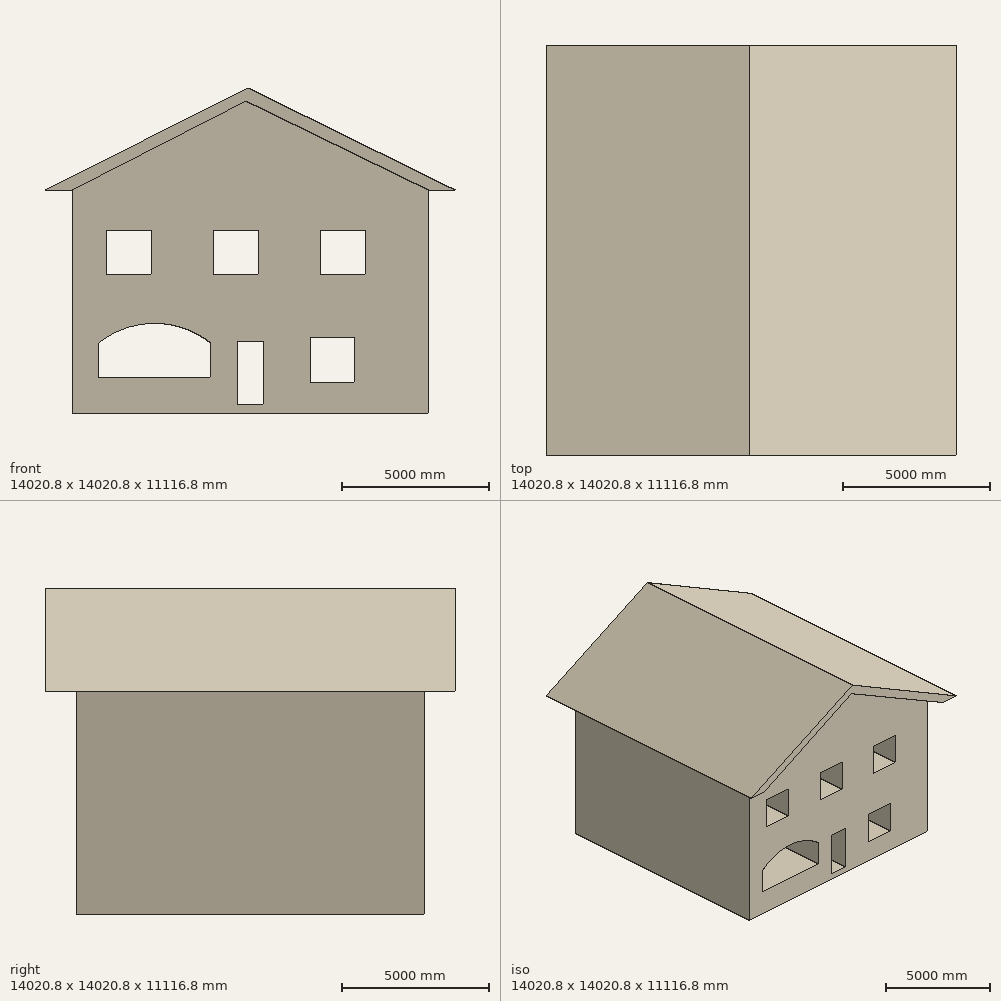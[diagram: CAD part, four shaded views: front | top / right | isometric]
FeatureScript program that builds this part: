
annotation { "Feature Type Name" : "Feature", "Feature Type Description" : "" }
export const myFeature = defineFeature(function(context is Context, id is Id, definition is map)
    precondition{}
    {
        {
            var Q0;
            Q0=qCreatedBy(makeId("Front.planeOp"),FACE);
            var sketch = newSketch(context, id + "F0", { "sketchPlane" : qUnion([Q0])});
            skLineSegment(sketch, "E0", {"start": v(0, 0) * mm, "end": v(-6096, 0) * mm});
            skLineSegment(sketch, "E1", {"start": v(0, 0) * mm, "end": v(6096, 0) * mm});
            skLineSegment(sketch, "E2", {"start": v(-6096, 0) * mm, "end": v(-147.95, 3044.4) * mm});
            skLineSegment(sketch, "E3", {"start": v(-147.95, 3044.4) * mm, "end": v(6096, 0) * mm});
            skLineSegment(sketch, "E4", {"start": v(-147.95, 3044.4) * mm, "end": v(0, 0) * mm, "construction": true});
            skLineSegment(sketch, "E5", {"start": v(-6096, 0) * mm, "end": v(-7010.4, 0) * mm});
            skLineSegment(sketch, "E6", {"start": v(6096, 0) * mm, "end": v(7010.4, 0) * mm});
            skLineSegment(sketch, "E7", {"start": v(-7010.4, 0) * mm, "end": v(-81.6, 3496.77) * mm});
            skLineSegment(sketch, "E8", {"start": v(7010.4, 0) * mm, "end": v(-81.6, 3496.77) * mm});
            skLineSegment(sketch, "E9", {"start": v(-147.95, 3044.4) * mm, "end": v(-81.6, 3496.77) * mm, "construction": true});
            skLineSegment(sketch, "E10", {"start": v(-6096, 0) * mm, "end": v(-6096, -7315.2) * mm});
            skLineSegment(sketch, "E11", {"start": v(6096, 0) * mm, "end": v(6096, -7315.2) * mm});
            skLineSegment(sketch, "E12", {"start": v(-6096, -7315.2) * mm, "end": v(6096, -7315.2) * mm});
            skLineSegment(sketch, "E13", {"start": v(-6096, -7315.2) * mm, "end": v(-6096, -7620) * mm});
            skLineSegment(sketch, "E14", {"start": v(6096, -7315.2) * mm, "end": v(6096, -7620) * mm});
            skLineSegment(sketch, "E15", {"start": v(-6096, -7620) * mm, "end": v(6096, -7620) * mm});
            skLineSegment(sketch, "E16", {"start": v(0, -7315.2) * mm, "end": v(-457.2, -7315.2) * mm});
            skLineSegment(sketch, "E17", {"start": v(0, -7315.2) * mm, "end": v(457.2, -7315.2) * mm});
            skLineSegment(sketch, "E18", {"start": v(457.2, -7315.2) * mm, "end": v(457.2, -5181.6) * mm});
            skLineSegment(sketch, "E19", {"start": v(457.2, -5181.6) * mm, "end": v(-457.2, -5181.6) * mm});
            skLineSegment(sketch, "E20", {"start": v(-457.2, -5181.6) * mm, "end": v(-457.2, -7315.2) * mm});
            skLineSegment(sketch, "E21", {"start": v(6096, -7315.2) * mm, "end": v(6096, -3657.6) * mm});
            skLineSegment(sketch, "E22", {"start": v(6096, -3657.6) * mm, "end": v(-6096, -3657.6) * mm, "construction": true});
            skLineSegment(sketch, "E23.bottom", {"start": v(-4757.74, -1524) * mm, "end": v(-3538.54, -1524) * mm});
            skLineSegment(sketch, "E23.top", {"start": v(-4757.74, -2743.2) * mm, "end": v(-3538.54, -2743.2) * mm});
            skLineSegment(sketch, "E23.left", {"start": v(-4757.74, -1524) * mm, "end": v(-4757.74, -2743.2) * mm});
            skLineSegment(sketch, "E23.right", {"start": v(-3538.54, -1524) * mm, "end": v(-3538.54, -2743.2) * mm});
            skLineSegment(sketch, "E24.bottom", {"start": v(-5185.84, -5232.23) * mm, "end": v(-1355.2, -5232.23) * mm});
            skLineSegment(sketch, "E24.top", {"start": v(-5185.84, -6400.8) * mm, "end": v(-1355.2, -6400.8) * mm});
            skLineSegment(sketch, "E24.left", {"start": v(-5185.84, -5232.23) * mm, "end": v(-5185.84, -6400.8) * mm});
            skLineSegment(sketch, "E24.right", {"start": v(-1355.2, -5232.23) * mm, "end": v(-1355.2, -6400.8) * mm});
            skLineSegment(sketch, "E25", {"start": v(-1355.2, -6400.8) * mm, "end": v(-1355.2, -7315.2) * mm, "construction": true});
            skLineSegment(sketch, "E26.bottom", {"start": v(2189.08, -6400.8) * mm, "end": v(3408.28, -6400.8) * mm});
            skLineSegment(sketch, "E26.top", {"start": v(2189.08, -5214.24) * mm, "end": v(3408.28, -5214.24) * mm});
            skLineSegment(sketch, "E26.left", {"start": v(2189.08, -6400.8) * mm, "end": v(2189.08, -5214.24) * mm});
            skLineSegment(sketch, "E26.right", {"start": v(3408.28, -6400.8) * mm, "end": v(3408.28, -5214.24) * mm});
            skLineSegment(sketch, "E27.bottom", {"start": v(2557.46, -2743.2) * mm, "end": v(3776.66, -2743.2) * mm});
            skLineSegment(sketch, "E27.top", {"start": v(2557.46, -1524) * mm, "end": v(3776.66, -1524) * mm});
            skLineSegment(sketch, "E27.left", {"start": v(2557.46, -1524) * mm, "end": v(2557.46, -2743.2) * mm});
            skLineSegment(sketch, "E27.right", {"start": v(3776.66, -1524) * mm, "end": v(3776.66, -2743.2) * mm});
            skLineSegment(sketch, "E28.bottom", {"start": v(-1100.14, -1524) * mm, "end": v(119.06, -1524) * mm});
            skLineSegment(sketch, "E28.top", {"start": v(-1100.14, -2743.2) * mm, "end": v(119.06, -2743.2) * mm});
            skLineSegment(sketch, "E28.left", {"start": v(-1100.14, -1524) * mm, "end": v(-1100.14, -2743.2) * mm});
            skLineSegment(sketch, "E28.right", {"start": v(119.06, -1524) * mm, "end": v(119.06, -2743.2) * mm});
            skLineSegment(sketch, "E29", {"start": v(-4757.74, -2743.2) * mm, "end": v(-4757.74, -3657.6) * mm, "construction": true});
            skLineSegment(sketch, "E30", {"start": v(-1100.14, -2743.2) * mm, "end": v(-1100.14, -3657.6) * mm, "construction": true});
            skLineSegment(sketch, "E31", {"start": v(2557.46, -2743.2) * mm, "end": v(2557.46, -3657.6) * mm, "construction": true});
            skLineSegment(sketch, "E32.bottom", {"start": v(271.46, -2895.6) * mm, "end": v(-1252.54, -2895.6) * mm});
            skLineSegment(sketch, "E32.top", {"start": v(271.46, -1371.6) * mm, "end": v(-1252.54, -1371.6) * mm});
            skLineSegment(sketch, "E32.left", {"start": v(271.46, -2895.6) * mm, "end": v(271.46, -1371.6) * mm});
            skLineSegment(sketch, "E32.right", {"start": v(-1252.54, -2895.6) * mm, "end": v(-1252.54, -1371.6) * mm});
            skPoint(sketch, "E32.middle", {"position": v(-490.54, -2133.6) * mm});
            skPoint(sketch, "E32.middle.positionSnap0", {"position": v(-490.54, -1524) * mm});
            skPoint(sketch, "E32.middle.positionSnap1", {"position": v(-1100.14, -2133.6) * mm});
            skPoint(sketch, "E32.centerSnap0", {"position": v(-490.54, -1524) * mm});
            skPoint(sketch, "E32.centerSnap1", {"position": v(-1100.14, -2133.6) * mm});
            skLineSegment(sketch, "E33.bottom", {"start": v(-3386.14, -2895.6) * mm, "end": v(-4910.14, -2895.6) * mm});
            skLineSegment(sketch, "E33.top", {"start": v(-3386.14, -1371.6) * mm, "end": v(-4910.14, -1371.6) * mm});
            skLineSegment(sketch, "E33.left", {"start": v(-3386.14, -2895.6) * mm, "end": v(-3386.14, -1371.6) * mm});
            skLineSegment(sketch, "E33.right", {"start": v(-4910.14, -2895.6) * mm, "end": v(-4910.14, -1371.6) * mm});
            skPoint(sketch, "E33.middle", {"position": v(-4148.14, -2133.6) * mm});
            skPoint(sketch, "E33.middle.positionSnap0", {"position": v(-4757.74, -2133.6) * mm});
            skPoint(sketch, "E33.middle.positionSnap1", {"position": v(-4148.14, -2743.2) * mm});
            skPoint(sketch, "E33.centerSnap0", {"position": v(-4757.74, -2133.6) * mm});
            skPoint(sketch, "E33.centerSnap1", {"position": v(-4148.14, -2743.2) * mm});
            skArc(sketch, "E34", {"start": v(-1355.2, -5232.23) * mm, "mid": v(-3270.52, -4555.28) * mm, "end": v(-5185.84, -5232.23) * mm});
            skLineSegment(sketch, "E35.bottom", {"start": v(3929.06, -2895.6) * mm, "end": v(2405.06, -2895.6) * mm});
            skLineSegment(sketch, "E35.top", {"start": v(3929.06, -1371.6) * mm, "end": v(2405.06, -1371.6) * mm});
            skLineSegment(sketch, "E35.left", {"start": v(3929.06, -2895.6) * mm, "end": v(3929.06, -1371.6) * mm});
            skLineSegment(sketch, "E35.right", {"start": v(2405.06, -2895.6) * mm, "end": v(2405.06, -1371.6) * mm});
            skPoint(sketch, "E35.middle", {"position": v(3167.06, -2133.6) * mm});
            skPoint(sketch, "E35.middle.positionSnap0", {"position": v(2557.46, -2133.6) * mm});
            skPoint(sketch, "E35.middle.positionSnap1", {"position": v(3167.06, -1524) * mm});
            skPoint(sketch, "E35.centerSnap0", {"position": v(2557.46, -2133.6) * mm});
            skPoint(sketch, "E35.centerSnap1", {"position": v(3167.06, -1524) * mm});
            skLineSegment(sketch, "E36.bottom", {"start": v(3560.68, -6569.52) * mm, "end": v(2036.68, -6569.52) * mm});
            skLineSegment(sketch, "E36.top", {"start": v(3560.68, -5045.52) * mm, "end": v(2036.68, -5045.52) * mm});
            skLineSegment(sketch, "E36.left", {"start": v(3560.68, -6569.52) * mm, "end": v(3560.68, -5045.52) * mm});
            skLineSegment(sketch, "E36.right", {"start": v(2036.68, -6569.52) * mm, "end": v(2036.68, -5045.52) * mm});
            skPoint(sketch, "E36.middle", {"position": v(2798.68, -5807.52) * mm});
            skPoint(sketch, "E36.middle.positionSnap0", {"position": v(2189.08, -5807.52) * mm});
            skPoint(sketch, "E36.middle.positionSnap1", {"position": v(2798.68, -5214.24) * mm});
            skPoint(sketch, "E36.centerSnap0", {"position": v(2189.08, -5807.52) * mm});
            skPoint(sketch, "E36.centerSnap1", {"position": v(2798.68, -5214.24) * mm});
            skLineSegment(sketch, "E37", {"start": v(3560.68, -6569.52) * mm, "end": v(3560.68, -7315.2) * mm, "construction": true});
            skLineSegment(sketch, "E38", {"start": v(3560.68, -7315.2) * mm, "end": v(3560.68, -6569.52) * mm, "construction": true});
            skLineSegment(sketch, "E39", {"start": v(2798.68, -5807.52) * mm, "end": v(2798.68, -7315.2) * mm, "construction": true});
            skSolve(sketch);
        }
        {
            var Q0;
            Q0=makeQuery(id+"F0.imprint","IMPRINT",FACE,{"disambiguationData":[TD([[makeQuery(id+"F0.imprint","IMPRINT",EDGE,{"derivedFrom":sQuery(id+"F0.wireOp",EDGE,"E2")}),1.0]])]});
            extrude(context, id + "F1", {"entities" : qUnion([Q0]), "endBound" : BoundingType.SYMMETRIC, "oppositeDirection" : true, "depth" : 14020.8 * mm, "offsetDistance" : 30.48 * mm});
        }
        {
            var Q0;
            Q0 = qSketchRegion(id + "F0", true);
            extrude(context, id + "F2", {"entities" : qUnion([Q0]), "operationType" : NewBodyOperationType.ADD, "endBound" : BoundingType.SYMMETRIC, "depth" : 11887.2 * mm, "offsetDistance" : 30.48 * mm});
        }
    });
